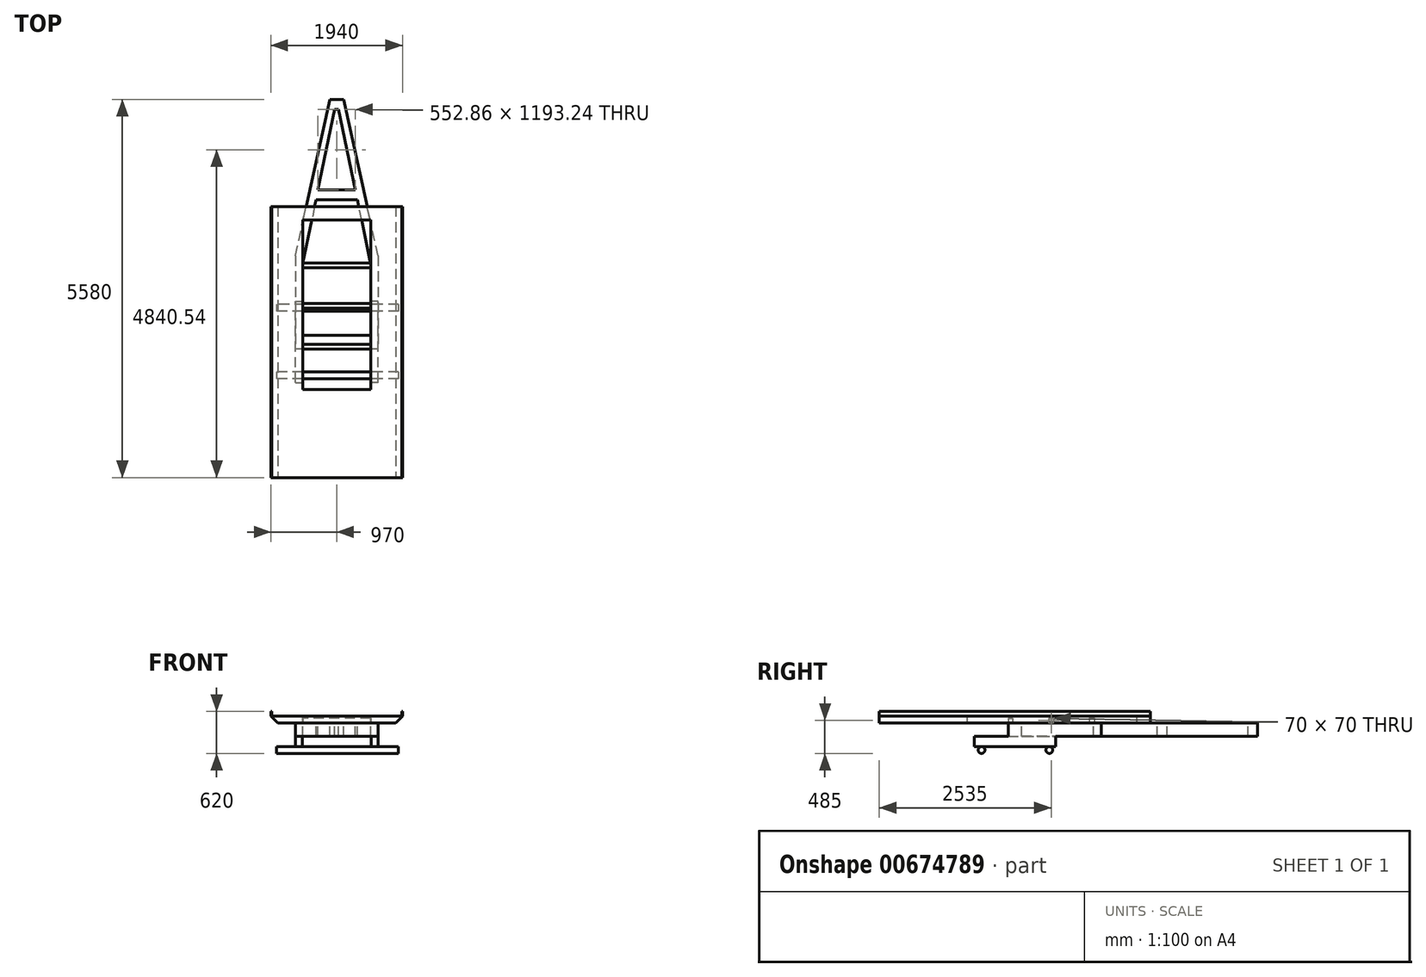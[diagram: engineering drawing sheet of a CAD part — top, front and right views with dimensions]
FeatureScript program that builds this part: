
annotation { "Feature Type Name" : "Feature", "Feature Type Description" : "" }
export const myFeature = defineFeature(function(context is Context, id is Id, definition is map)
    precondition{}
    {
        {
            var Q0;
            Q0=qCreatedBy(makeId("Front.planeOp"),FACE);
            var sketch = newSketch(context, id + "F0", { "sketchPlane" : qUnion([Q0])});
            skLineSegment(sketch, "E0.bottom", {"start": v(100, 0) * mm, "end": v(1840, 0) * mm});
            skLineSegment(sketch, "E0.top", {"start": v(0, 100) * mm, "end": v(1940, 100) * mm});
            skLineSegment(sketch, "E1", {"start": v(0, 100) * mm, "end": v(100, 0) * mm});
            skLineSegment(sketch, "E2", {"start": v(1940, 100) * mm, "end": v(1840, 0) * mm});
            skSolve(sketch);
        }
        {
            var Q0;
            Q0=makeQuery(id+"F0.imprint","IMPRINT",FACE,{"disambiguationData":[TD([[makeQuery(id+"F0.imprint","IMPRINT",EDGE,{"derivedFrom":sQuery(id+"F0.wireOp",EDGE,"E0.bottom")}),1.0]])]});
            extrude(context, id + "F1", {"entities" : qUnion([Q0]), "oppositeDirection" : true, "depth" : 4000 * mm, "offsetDistance" : 25 * mm});
        }
        {
            var Q0;
            Q0=makeQuery(id+"F1.opExtrude","SWEPT_FACE",FACE,{"disambiguationData":[OSD([sQuery(id+"F0.wireOp",EDGE,"E0.top")])]});
            var sketch = newSketch(context, id + "F2", { "sketchPlane" : qUnion([Q0])});
            skLineSegment(sketch, "E3.bottom", {"start": v(470, 3800) * mm, "end": v(1470, 3800) * mm});
            skLineSegment(sketch, "E3.top", {"start": v(470, 1300) * mm, "end": v(1470, 1300) * mm});
            skLineSegment(sketch, "E3.left", {"start": v(470, 3800) * mm, "end": v(470, 1300) * mm});
            skLineSegment(sketch, "E3.right", {"start": v(1470, 3800) * mm, "end": v(1470, 1300) * mm});
            skSolve(sketch);
        }
        {
            var Q0;
            Q0=makeQuery(id+"F2.imprint","IMPRINT",FACE,{"disambiguationData":[TD([[makeQuery(id+"F2.imprint","IMPRINT",EDGE,{"derivedFrom":sQuery(id+"F2.wireOp",EDGE,"E3.bottom")}),-1.0]])]});
            extrude(context, id + "F3", {"entities" : qUnion([Q0]), "operationType" : NewBodyOperationType.REMOVE, "oppositeDirection" : true, "depth" : 100 * mm, "offsetDistance" : 25 * mm});
        }
        {
            var Q0;
            Q0=makeQuery(id+"F3.boolean.opBoolean","COPY",FACE,{"derivedFrom":makeQuery(id+"F3.opExtrude","SWEPT_FACE",FACE,{"disambiguationData":[OSD([sQuery(id+"F2.wireOp",EDGE,"E3.left")])]})});
            var sketch = newSketch(context, id + "F4", { "sketchPlane" : qUnion([Q0])});
            skLineSegment(sketch, "E4.bottom", {"start": v(1900, 70) * mm, "end": v(1970, 70) * mm});
            skLineSegment(sketch, "E4.top", {"start": v(1900, 0) * mm, "end": v(1970, 0) * mm});
            skLineSegment(sketch, "E4.left", {"start": v(1900, 70) * mm, "end": v(1900, 0) * mm});
            skLineSegment(sketch, "E4.right", {"start": v(1970, 70) * mm, "end": v(1970, 0) * mm});
            skLineSegment(sketch, "E5.1.0.0", {"start": v(2500, 70) * mm, "end": v(2570, 70) * mm});
            skLineSegment(sketch, "E5.1.0.1", {"start": v(2570, 70) * mm, "end": v(2570, 0) * mm});
            skLineSegment(sketch, "E5.1.0.2", {"start": v(2500, 70) * mm, "end": v(2500, 0) * mm});
            skLineSegment(sketch, "E5.1.0.3", {"start": v(2500, 0) * mm, "end": v(2570, 0) * mm});
            skLineSegment(sketch, "E5.2.0.0", {"start": v(3100, 70) * mm, "end": v(3170, 70) * mm});
            skLineSegment(sketch, "E5.2.0.1", {"start": v(3170, 70) * mm, "end": v(3170, 0) * mm});
            skLineSegment(sketch, "E5.2.0.2", {"start": v(3100, 70) * mm, "end": v(3100, 0) * mm});
            skLineSegment(sketch, "E5.2.0.3", {"start": v(3100, 0) * mm, "end": v(3170, 0) * mm});
            skLineSegment(sketch, "E5.direction1", {"start": v(1900, 0) * mm, "end": v(2500, 0) * mm, "construction": true});
            skSolve(sketch);
        }
        {
            var Q0;
            Q0 = qSketchRegion(id + "F4", true);
            extrude(context, id + "F5", {"entities" : qUnion([Q0]), "operationType" : NewBodyOperationType.ADD, "depth" : 1000 * mm, "offsetDistance" : 25 * mm});
        }
        {
            var Q0;
            Q0=makeQuery(id+"F1.opExtrude","SWEPT_FACE",FACE,{"disambiguationData":[OSD([sQuery(id+"F0.wireOp",EDGE,"E0.top")])]});
            var sketch = newSketch(context, id + "F6", { "sketchPlane" : qUnion([Q0])});
            skLineSegment(sketch, "E6.bottom", {"start": v(0, 0) * mm, "end": v(10, 0) * mm});
            skLineSegment(sketch, "E6.top", {"start": v(0, 4000) * mm, "end": v(10, 4000) * mm});
            skLineSegment(sketch, "E6.left", {"start": v(0, 0) * mm, "end": v(0, 4000) * mm});
            skLineSegment(sketch, "E6.right", {"start": v(10, 0) * mm, "end": v(10, 4000) * mm});
            skLineSegment(sketch, "E7.bottom", {"start": v(1940, 0) * mm, "end": v(1930, 0) * mm});
            skLineSegment(sketch, "E7.top", {"start": v(1940, 4000) * mm, "end": v(1930, 4000) * mm});
            skLineSegment(sketch, "E7.left", {"start": v(1940, 0) * mm, "end": v(1940, 4000) * mm});
            skLineSegment(sketch, "E7.right", {"start": v(1930, 0) * mm, "end": v(1930, 4000) * mm});
            skSolve(sketch);
        }
        {
            var Q0;
            Q0 = qSketchRegion(id + "F6", true);
            extrude(context, id + "F7", {"entities" : qUnion([Q0]), "operationType" : NewBodyOperationType.ADD, "depth" : 70 * mm, "offsetDistance" : 25 * mm});
        }
        {
            var Q0;
            Q0=makeQuery(id+"F5.boolean.opBoolean","MERGE",FACE,{"derivedFrom":[makeQuery(id+"F1.opExtrude","SWEPT_FACE",FACE,{"disambiguationData":[OSD([sQuery(id+"F0.wireOp",EDGE,"E0.bottom")])]}),makeQuery(id+"F5.opExtrude","SWEPT_FACE",FACE,{"disambiguationData":[OSD([sQuery(id+"F4.wireOp",EDGE,"E4.top")])]}),makeQuery(id+"F5.opExtrude","SWEPT_FACE",FACE,{"disambiguationData":[OSD([sQuery(id+"F4.wireOp",EDGE,"E5.1.0.3")])]}),makeQuery(id+"F5.opExtrude","SWEPT_FACE",FACE,{"disambiguationData":[OSD([sQuery(id+"F4.wireOp",EDGE,"E5.2.0.3")])]})]});
            var sketch = newSketch(context, id + "F8", { "sketchPlane" : qUnion([Q0])});
            skLineSegment(sketch, "E8.bottom", {"start": v(1580.08, -1900) * mm, "end": v(359.92, -1900) * mm});
            skLineSegment(sketch, "E8.top", {"start": v(1470, -2100) * mm, "end": v(470, -2100) * mm});
            skLineSegment(sketch, "E9", {"start": v(359.92, -3274.73) * mm, "end": v(870, -5580) * mm});
            skLineSegment(sketch, "E10", {"start": v(1580.08, -3274.73) * mm, "end": v(1070, -5580) * mm});
            skLineSegment(sketch, "E11", {"start": v(1070, -5580) * mm, "end": v(870, -5580) * mm});
            skLineSegment(sketch, "E12", {"start": v(1470, -3163.33) * mm, "end": v(1276.33, -4099.42) * mm});
            skLineSegment(sketch, "E13", {"start": v(940.45, -5437.16) * mm, "end": v(693.57, -4243.93) * mm});
            skLineSegment(sketch, "E14", {"start": v(999.55, -5437.16) * mm, "end": v(940.45, -5437.16) * mm});
            skLineSegment(sketch, "E15.bottom", {"start": v(1276.33, -4099.42) * mm, "end": v(663.67, -4099.42) * mm});
            skLineSegment(sketch, "E15.top", {"start": v(1246.43, -4243.93) * mm, "end": v(693.57, -4243.93) * mm});
            skLineSegment(sketch, "E16.trimOffspring", {"start": v(1246.43, -4243.93) * mm, "end": v(999.55, -5437.16) * mm});
            skLineSegment(sketch, "E17.trimOffspring", {"start": v(663.67, -4099.42) * mm, "end": v(470, -3163.33) * mm});
            skPoint(sketch, "E18.orphan", {"position": v(970, -5580) * mm});
            skLineSegment(sketch, "E19", {"start": v(1580.08, -3274.73) * mm, "end": v(1580.08, -1900) * mm});
            skLineSegment(sketch, "E20", {"start": v(359.92, -3274.73) * mm, "end": v(359.92, -1900) * mm});
            skLineSegment(sketch, "E21", {"start": v(1470, -2100) * mm, "end": v(1470, -3170) * mm});
            skLineSegment(sketch, "E22", {"start": v(470, -2100) * mm, "end": v(470, -3170) * mm});
            skPoint(sketch, "E8.left.end.orphan", {"position": v(1840, -2100) * mm});
            skPoint(sketch, "E23.orphan", {"position": v(1690, -2100) * mm});
            skPoint(sketch, "E8.right.end.orphan", {"position": v(100, -2100) * mm});
            skPoint(sketch, "E24.orphan", {"position": v(250, -2100) * mm});
            skSolve(sketch);
        }
        {
            var Q0;
            Q0 = qSketchRegion(id + "F8", true);
            extrude(context, id + "F9", {"entities" : qUnion([Q0]), "operationType" : NewBodyOperationType.ADD, "depth" : 200 * mm, "offsetDistance" : 25 * mm});
        }
        {
            var Q0;
            Q0=makeQuery(id+"F9.opExtrude","CAP_FACE",FACE,{"disambiguationData":[OSD([sQuery(id+"F8.wireOp",EDGE,"E8.bottom"),sQuery(id+"F8.wireOp",EDGE,"E8.top"),sQuery(id+"F8.wireOp",EDGE,"E9"),sQuery(id+"F8.wireOp",EDGE,"E10"),sQuery(id+"F8.wireOp",EDGE,"E11"),sQuery(id+"F8.wireOp",EDGE,"E12"),sQuery(id+"F8.wireOp",EDGE,"E13"),sQuery(id+"F8.wireOp",EDGE,"E14"),sQuery(id+"F8.wireOp",EDGE,"E15.bottom"),sQuery(id+"F8.wireOp",EDGE,"E15.top"),sQuery(id+"F8.wireOp",EDGE,"E16.trimOffspring"),sQuery(id+"F8.wireOp",EDGE,"E17.trimOffspring"),sQuery(id+"F8.wireOp",EDGE,"E19"),sQuery(id+"F8.wireOp",EDGE,"E20"),sQuery(id+"F8.wireOp",EDGE,"E21"),sQuery(id+"F8.wireOp",EDGE,"E22")])],"isStart":false});
            var sketch = newSketch(context, id + "F10", { "sketchPlane" : qUnion([Q0])});
            skLineSegment(sketch, "E25.bottom", {"start": v(1580.08, -1400) * mm, "end": v(1480.08, -1400) * mm});
            skLineSegment(sketch, "E25.top", {"start": v(1580.08, -2600) * mm, "end": v(1480.08, -2600) * mm});
            skLineSegment(sketch, "E25.left", {"start": v(1580.08, -1400) * mm, "end": v(1580.08, -2600) * mm});
            skLineSegment(sketch, "E25.right", {"start": v(1480.08, -1400) * mm, "end": v(1480.08, -2600) * mm});
            skLineSegment(sketch, "E26.bottom", {"start": v(359.92, -1400) * mm, "end": v(459.92, -1400) * mm});
            skLineSegment(sketch, "E26.top", {"start": v(359.92, -2600) * mm, "end": v(459.92, -2600) * mm});
            skLineSegment(sketch, "E26.left", {"start": v(359.92, -1400) * mm, "end": v(359.92, -2600) * mm});
            skLineSegment(sketch, "E26.right", {"start": v(459.92, -1400) * mm, "end": v(459.92, -2600) * mm});
            skSolve(sketch);
        }
        {
            var Q0;
            {var subQ0=sQuery(id+"F10.wireOp",EDGE,"E25.bottom");Q0=makeQuery(id+"F10.imprint","IMPRINT",FACE,{"disambiguationData":[TD([[makeQuery(id+"F10.imprint","IMPRINT",EDGE,{"derivedFrom":subQ0}),1.0]])]});}
            var Q1;
            {var subQ0=sQuery(id+"F10.wireOp",EDGE,"E25.top");Q1=makeQuery(id+"F10.imprint","IMPRINT",FACE,{"disambiguationData":[TD([[makeQuery(id+"F10.imprint","IMPRINT",EDGE,{"derivedFrom":subQ0}),-1.0]])]});}
            var Q2;
            {var subQ0=sQuery(id+"F10.wireOp",EDGE,"E26.bottom");Q2=makeQuery(id+"F10.imprint","IMPRINT",FACE,{"disambiguationData":[TD([[makeQuery(id+"F10.imprint","IMPRINT",EDGE,{"derivedFrom":subQ0}),-1.0]])]});}
            var Q3;
            {var subQ0=sQuery(id+"F10.wireOp",EDGE,"E26.top");Q3=makeQuery(id+"F10.imprint","IMPRINT",FACE,{"disambiguationData":[TD([[makeQuery(id+"F10.imprint","IMPRINT",EDGE,{"derivedFrom":subQ0}),1.0]])]});}
            extrude(context, id + "F11", {"entities" : qUnion([Q0, Q1, Q2, Q3]), "operationType" : NewBodyOperationType.ADD, "depth" : 150 * mm, "offsetDistance" : 25 * mm});
        }
        {
            var Q0;
            Q0=makeQuery(id+"F11.boolean.opBoolean","MERGE",FACE,{"derivedFrom":[makeQuery(id+"F9.opExtrude","SWEPT_FACE",FACE,{"disambiguationData":[OSD([sQuery(id+"F8.wireOp",EDGE,"E19")])]}),makeQuery(id+"F11.opExtrude","SWEPT_FACE",FACE,{"disambiguationData":[OSD([sQuery(id+"F10.wireOp",EDGE,"E25.left")])]})]});
            var sketch = newSketch(context, id + "F12", { "sketchPlane" : qUnion([Q0])});
            skCircle(sketch, "E27", {"center": v(1508.27, -400) * mm, "radius": 50 * mm});
            skCircle(sketch, "E28", {"center": v(2508.27, -400) * mm, "radius": 50 * mm});
            skSolve(sketch);
        }
        {
            var Q0;
            Q0 = qSketchRegion(id + "F12", true);
            extrude(context, id + "F13", {"entities" : qUnion([Q0]), "operationType" : NewBodyOperationType.ADD, "depth" : 300 * mm, "offsetDistance" : 25 * mm, "hasSecondDirection" : true, "secondDirectionOppositeDirection" : true, "secondDirectionDepth" : 1500 * mm});
        }
    });
